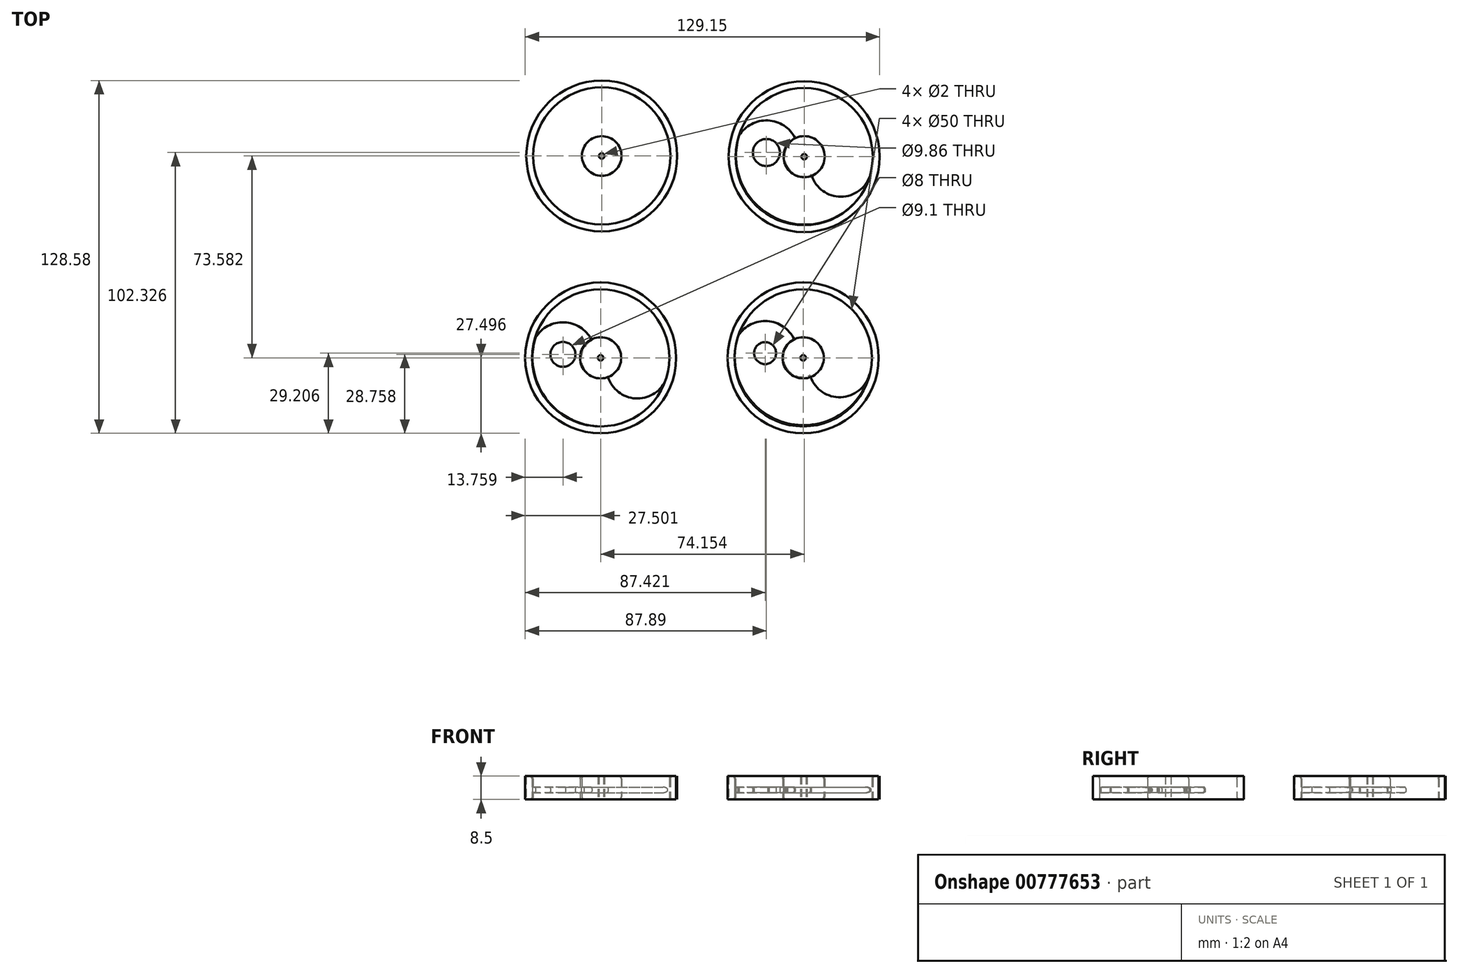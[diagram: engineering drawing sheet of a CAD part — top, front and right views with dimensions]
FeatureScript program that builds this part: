
annotation { "Feature Type Name" : "Feature", "Feature Type Description" : "" }
export const myFeature = defineFeature(function(context is Context, id is Id, definition is map)
    precondition{}
    {
        {
            var Q0;
            Q0=qCreatedBy(makeId("Top.planeOp"),FACE);
            var sketch = newSketch(context, id + "F0", { "sketchPlane" : qUnion([Q0])});
            skCircle(sketch, "E0", {"center": v(-36.84, 37.34) * mm, "radius": 27.5 * mm});
            skCircle(sketch, "E1", {"center": v(36.9, 37.09) * mm, "radius": 27.5 * mm});
            skCircle(sketch, "E2", {"center": v(36.55, -36.24) * mm, "radius": 27.5 * mm});
            skCircle(sketch, "E3", {"center": v(-37.25, -36.24) * mm, "radius": 27.5 * mm});
            skCircle(sketch, "E4", {"center": v(-36.84, 37.34) * mm, "radius": 25 * mm});
            skCircle(sketch, "E5", {"center": v(36.9, 37.09) * mm, "radius": 25 * mm});
            skCircle(sketch, "E6", {"center": v(-37.25, -36.24) * mm, "radius": 25 * mm});
            skCircle(sketch, "E7", {"center": v(36.55, -36.24) * mm, "radius": 25 * mm});
            skCircle(sketch, "E8", {"center": v(-36.84, 37.34) * mm, "radius": 7.22 * mm});
            skCircle(sketch, "E9", {"center": v(-36.84, 37.34) * mm, "radius": 1 * mm});
            skCircle(sketch, "E10", {"center": v(36.9, 37.09) * mm, "radius": 7.5 * mm});
            skCircle(sketch, "E11", {"center": v(-37.25, -36.24) * mm, "radius": 7.5 * mm});
            skCircle(sketch, "E12", {"center": v(36.55, -36.24) * mm, "radius": 7.5 * mm});
            skCircle(sketch, "E13", {"center": v(-37.25, -36.24) * mm, "radius": 1 * mm});
            skCircle(sketch, "E14", {"center": v(36.55, -36.24) * mm, "radius": 1 * mm});
            skCircle(sketch, "E15", {"center": v(36.9, 37.09) * mm, "radius": 1 * mm});
            skCircle(sketch, "E16", {"center": v(-36.84, 37.34) * mm, "radius": 24.87 * mm});
            skSolve(sketch);
        }
        {
            var Q0;
            Q0 = qSketchRegion(id + "F0", true);
            var Q1;
            Q1=makeQuery(id+"F0.imprint","IMPRINT",FACE,{"disambiguationData":[TD([[makeQuery(id+"F0.imprint","IMPRINT",EDGE,{"derivedFrom":sQuery(id+"F0.wireOp",EDGE,"E8")}),1.0]])]});
            var Q2;
            Q2=makeQuery(id+"F0.imprint","IMPRINT",FACE,{"disambiguationData":[TD([[makeQuery(id+"F0.imprint","IMPRINT",EDGE,{"derivedFrom":sQuery(id+"F0.wireOp",EDGE,"E10")}),1.0]])]});
            var Q3;
            Q3=makeQuery(id+"F0.imprint","IMPRINT",FACE,{"disambiguationData":[TD([[makeQuery(id+"F0.imprint","IMPRINT",EDGE,{"derivedFrom":sQuery(id+"F0.wireOp",EDGE,"E12")}),1.0]])]});
            var Q4;
            Q4=makeQuery(id+"F0.imprint","IMPRINT",FACE,{"disambiguationData":[TD([[makeQuery(id+"F0.imprint","IMPRINT",EDGE,{"derivedFrom":sQuery(id+"F0.wireOp",EDGE,"E11")}),1.0]])]});
            extrude(context, id + "F1", {"entities" : qUnion([Q0, Q1, Q2, Q3, Q4]), "depth" : 5 * mm, "offsetDistance" : 25 * mm, "hasSecondDirection" : true, "secondDirectionOppositeDirection" : true, "secondDirectionDepth" : 3.5 * mm});
        }
        {
            var Q0;
            Q0=makeQuery(id+"F1.opExtrude","CAP_EDGE",EDGE,{"disambiguationData":[OSD([sQuery(id+"F0.wireOp",EDGE,"E4")])],"isStart":false});
            var Q1;
            Q1=makeQuery(id+"F1.opExtrude","CAP_EDGE",EDGE,{"disambiguationData":[OSD([sQuery(id+"F0.wireOp",EDGE,"E5")])],"isStart":false});
            var Q2;
            Q2=makeQuery(id+"F1.opExtrude","CAP_EDGE",EDGE,{"disambiguationData":[OSD([sQuery(id+"F0.wireOp",EDGE,"E7")])],"isStart":false});
            var Q3;
            Q3=makeQuery(id+"F1.opExtrude","CAP_EDGE",EDGE,{"disambiguationData":[OSD([sQuery(id+"F0.wireOp",EDGE,"E8")])],"isStart":false});
            var Q4;
            Q4=makeQuery(id+"F1.opExtrude","CAP_EDGE",EDGE,{"disambiguationData":[OSD([sQuery(id+"F0.wireOp",EDGE,"E10")])],"isStart":false});
            var Q5;
            Q5=makeQuery(id+"F1.opExtrude","CAP_EDGE",EDGE,{"disambiguationData":[OSD([sQuery(id+"F0.wireOp",EDGE,"E12")])],"isStart":false});
            var Q6;
            Q6=makeQuery(id+"F1.opExtrude","CAP_EDGE",EDGE,{"disambiguationData":[OSD([sQuery(id+"F0.wireOp",EDGE,"E11")])],"isStart":false});
            var Q7;
            Q7=makeQuery(id+"F1.opExtrude","CAP_EDGE",EDGE,{"disambiguationData":[OSD([sQuery(id+"F0.wireOp",EDGE,"E11")])],"isStart":true});
            var Q8;
            Q8=makeQuery(id+"F1.opExtrude","CAP_EDGE",EDGE,{"disambiguationData":[OSD([sQuery(id+"F0.wireOp",EDGE,"E6")])],"isStart":true});
            var Q9;
            Q9=makeQuery(id+"F1.opExtrude","CAP_EDGE",EDGE,{"disambiguationData":[OSD([sQuery(id+"F0.wireOp",EDGE,"E7")])],"isStart":true});
            var Q10;
            Q10=makeQuery(id+"F1.opExtrude","CAP_EDGE",EDGE,{"disambiguationData":[OSD([sQuery(id+"F0.wireOp",EDGE,"E5")])],"isStart":true});
            var Q11;
            Q11=makeQuery(id+"F1.opExtrude","CAP_EDGE",EDGE,{"disambiguationData":[OSD([sQuery(id+"F0.wireOp",EDGE,"E10")])],"isStart":true});
            var Q12;
            Q12=makeQuery(id+"F1.opExtrude","CAP_EDGE",EDGE,{"disambiguationData":[OSD([sQuery(id+"F0.wireOp",EDGE,"E12")])],"isStart":true});
            var Q13;
            Q13=makeQuery(id+"F1.opExtrude","CAP_EDGE",EDGE,{"disambiguationData":[OSD([sQuery(id+"F0.wireOp",EDGE,"E8")])],"isStart":true});
            var Q14;
            Q14=makeQuery(id+"F1.opExtrude","CAP_EDGE",EDGE,{"disambiguationData":[OSD([sQuery(id+"F0.wireOp",EDGE,"E6")])],"isStart":false});
            var Q15;
            Q15=makeQuery(id+"F1.opExtrude","CAP_EDGE",EDGE,{"disambiguationData":[OSD([sQuery(id+"F0.wireOp",EDGE,"E4")])],"isStart":true});
            fillet(context, id + "F2", {"entities" : qUnion([Q0, Q1, Q2, Q3, Q4, Q5, Q6, Q7, Q8, Q9, Q10, Q11, Q12, Q13, Q14, Q15]), "radius" : 1 * mm, "tangentPropagation" : true, "allowEdgeOverflow" : false});
        }
        {
            var Q0;
            Q0=qCreatedBy(makeId("Top.planeOp"),FACE);
            var sketch = newSketch(context, id + "F3", { "sketchPlane" : qUnion([Q0])});
            skArc(sketch, "E17", {"start": v(39.54, 30.51) * mm, "mid": v(50.51, 22.5) * mm, "end": v(61.15, 30.94) * mm});
            skArc(sketch, "E18", {"start": v(33.7, 43.68) * mm, "mid": v(23.79, 50.28) * mm, "end": v(13.22, 44.81) * mm});
            skArc(sketch, "E19", {"start": v(13.22, 44.81) * mm, "mid": v(13.67, 28.53) * mm, "end": v(24.09, 16.02) * mm});
            skArc(sketch, "E20", {"start": v(24.09, 16.02) * mm, "mid": v(46.4, 14.1) * mm, "end": v(61.15, 30.94) * mm});
            skArc(sketch, "E21", {"start": v(30.86, 33.25) * mm, "mid": v(34.68, 30.25) * mm, "end": v(39.54, 30.51) * mm});
            skArc(sketch, "E22", {"start": v(33.7, 43.68) * mm, "mid": v(30.07, 39.06) * mm, "end": v(30.86, 33.25) * mm});
            skCircle(sketch, "E23", {"center": v(23.14, 38.59) * mm, "radius": 4.93 * mm});
            skSolve(sketch);
        }
        {
            var Q0;
            Q0 = qSketchRegion(id + "F3", true);
            extrude(context, id + "F4", {"entities" : qUnion([Q0]), "depth" : 1 * mm, "offsetDistance" : 25 * mm, "hasSecondDirection" : true, "secondDirectionOppositeDirection" : true, "secondDirectionDepth" : 1 * mm});
        }
        {
            var Q0;
            Q0=qCreatedBy(makeId("Top.planeOp"),FACE);
            var sketch = newSketch(context, id + "F5", { "sketchPlane" : qUnion([Q0])});
            skArc(sketch, "E24", {"start": v(-34.6, -43.06) * mm, "mid": v(-23.62, -51.08) * mm, "end": v(-12.98, -42.62) * mm});
            skArc(sketch, "E25", {"start": v(-40.44, -29.9) * mm, "mid": v(-50.34, -23.28) * mm, "end": v(-60.92, -28.76) * mm});
            skArc(sketch, "E26", {"start": v(-60.92, -28.76) * mm, "mid": v(-60.46, -45.03) * mm, "end": v(-50.04, -57.55) * mm});
            skArc(sketch, "E27", {"start": v(-50.04, -57.55) * mm, "mid": v(-27.73, -59.47) * mm, "end": v(-12.98, -42.62) * mm});
            skArc(sketch, "E28", {"start": v(-43.27, -40.32) * mm, "mid": v(-39.45, -43.32) * mm, "end": v(-34.6, -43.06) * mm});
            skArc(sketch, "E29", {"start": v(-40.44, -29.9) * mm, "mid": v(-44.06, -34.5) * mm, "end": v(-43.27, -40.32) * mm});
            skCircle(sketch, "E30", {"center": v(-51, -34.98) * mm, "radius": 4.55 * mm});
            skSolve(sketch);
        }
        {
            var Q0;
            Q0 = qSketchRegion(id + "F5", true);
            extrude(context, id + "F6", {"entities" : qUnion([Q0]), "depth" : 1 * mm, "offsetDistance" : 25 * mm, "hasSecondDirection" : true, "secondDirectionOppositeDirection" : true, "secondDirectionDepth" : 1 * mm});
        }
        {
            var Q0;
            Q0=qCreatedBy(makeId("Top.planeOp"),FACE);
            var sketch = newSketch(context, id + "F7", { "sketchPlane" : qUnion([Q0])});
            skArc(sketch, "E31", {"start": v(39.07, -42.6) * mm, "mid": v(50.04, -50.63) * mm, "end": v(60.69, -42.18) * mm});
            skArc(sketch, "E32", {"start": v(33.22, -29.44) * mm, "mid": v(23.32, -22.84) * mm, "end": v(12.75, -28.3) * mm});
            skArc(sketch, "E33", {"start": v(12.75, -28.3) * mm, "mid": v(13.2, -44.59) * mm, "end": v(23.62, -57.1) * mm});
            skArc(sketch, "E34", {"start": v(23.62, -57.1) * mm, "mid": v(45.93, -59.02) * mm, "end": v(60.69, -42.18) * mm});
            skArc(sketch, "E35", {"start": v(30.4, -39.87) * mm, "mid": v(34.21, -42.87) * mm, "end": v(39.07, -42.6) * mm});
            skArc(sketch, "E36", {"start": v(33.22, -29.44) * mm, "mid": v(29.6, -34.06) * mm, "end": v(30.4, -39.87) * mm});
            skCircle(sketch, "E37", {"center": v(22.67, -34.53) * mm, "radius": 4 * mm});
            skSolve(sketch);
        }
        {
            var Q0;
            Q0 = qSketchRegion(id + "F7", true);
            extrude(context, id + "F8", {"entities" : qUnion([Q0]), "depth" : 1 * mm, "offsetDistance" : 25 * mm, "hasSecondDirection" : true, "secondDirectionOppositeDirection" : true, "secondDirectionDepth" : 1 * mm});
        }
        {
            var Q0;
            Q0=makeQuery(id+"F6.opExtrude","CAP_EDGE",EDGE,{"disambiguationData":[OSD([sQuery(id+"F5.wireOp",EDGE,"E24")])],"isStart":true});
            var Q1;
            Q1=makeQuery(id+"F6.opExtrude","CAP_EDGE",EDGE,{"disambiguationData":[OSD([sQuery(id+"F5.wireOp",EDGE,"E24")])],"isStart":false});
            var Q2;
            Q2=makeQuery(id+"F6.opExtrude","CAP_EDGE",EDGE,{"disambiguationData":[OSD([sQuery(id+"F5.wireOp",EDGE,"E25")])],"isStart":true});
            var Q3;
            Q3=makeQuery(id+"F6.opExtrude","CAP_EDGE",EDGE,{"disambiguationData":[OSD([sQuery(id+"F5.wireOp",EDGE,"E25")])],"isStart":false});
            var Q4;
            Q4=makeQuery(id+"F8.opExtrude","CAP_EDGE",EDGE,{"disambiguationData":[OSD([sQuery(id+"F7.wireOp",EDGE,"E31")])],"isStart":true});
            var Q5;
            Q5=makeQuery(id+"F8.opExtrude","CAP_EDGE",EDGE,{"disambiguationData":[OSD([sQuery(id+"F7.wireOp",EDGE,"E31")])],"isStart":false});
            var Q6;
            Q6=makeQuery(id+"F8.opExtrude","CAP_EDGE",EDGE,{"disambiguationData":[OSD([sQuery(id+"F7.wireOp",EDGE,"E32")])],"isStart":true});
            var Q7;
            Q7=makeQuery(id+"F8.opExtrude","CAP_EDGE",EDGE,{"disambiguationData":[OSD([sQuery(id+"F7.wireOp",EDGE,"E32")])],"isStart":false});
            var Q8;
            Q8=makeQuery(id+"F6.opExtrude","CAP_EDGE",EDGE,{"disambiguationData":[OSD([sQuery(id+"F5.wireOp",EDGE,"E30")])],"isStart":true});
            var Q9;
            Q9=makeQuery(id+"F6.opExtrude","CAP_EDGE",EDGE,{"disambiguationData":[OSD([sQuery(id+"F5.wireOp",EDGE,"E30")])],"isStart":false});
            var Q10;
            Q10=makeQuery(id+"F8.opExtrude","CAP_EDGE",EDGE,{"disambiguationData":[OSD([sQuery(id+"F7.wireOp",EDGE,"E37")])],"isStart":true});
            var Q11;
            Q11=makeQuery(id+"F8.opExtrude","CAP_EDGE",EDGE,{"disambiguationData":[OSD([sQuery(id+"F7.wireOp",EDGE,"E37")])],"isStart":false});
            var Q12;
            Q12=makeQuery(id+"F0Lw73LTv5gNUkS_8.opExtrude","CAP_EDGE",EDGE,{"disambiguationData":[OSD([sQuery(id+"FaSVQBoLKEiFSzY_8.wireOp",EDGE,"Rkogj6an-mIMs-5Vwq-ItiI-HnNTVvaIVaFF")])],"isStart":true});
            var Q13;
            Q13=makeQuery(id+"F0Lw73LTv5gNUkS_8.opExtrude","CAP_EDGE",EDGE,{"disambiguationData":[OSD([sQuery(id+"FaSVQBoLKEiFSzY_8.wireOp",EDGE,"0PIxKRfm-EENJ-GXSr-GtYf-4HL3wGRdEfpe")])],"isStart":true});
            var Q14;
            Q14=makeQuery(id+"F0Lw73LTv5gNUkS_8.opExtrude","CAP_EDGE",EDGE,{"disambiguationData":[OSD([sQuery(id+"FaSVQBoLKEiFSzY_8.wireOp",EDGE,"vxq344Cw-Kjq4-zHd9-gQkO-X8a2N7v6S6Nq")])],"isStart":true});
            var Q15;
            Q15=makeQuery(id+"F4.opExtrude","CAP_EDGE",EDGE,{"disambiguationData":[OSD([sQuery(id+"F3.wireOp",EDGE,"E23")])],"isStart":true});
            var Q16;
            Q16=makeQuery(id+"F4.opExtrude","CAP_EDGE",EDGE,{"disambiguationData":[OSD([sQuery(id+"F3.wireOp",EDGE,"E18")])],"isStart":true});
            var Q17;
            Q17=makeQuery(id+"F4.opExtrude","CAP_EDGE",EDGE,{"disambiguationData":[OSD([sQuery(id+"F3.wireOp",EDGE,"E17")])],"isStart":true});
            var Q18;
            Q18=makeQuery(id+"F0Lw73LTv5gNUkS_8.opExtrude","CAP_EDGE",EDGE,{"disambiguationData":[OSD([sQuery(id+"FaSVQBoLKEiFSzY_8.wireOp",EDGE,"vxq344Cw-Kjq4-zHd9-gQkO-X8a2N7v6S6Nq")])],"isStart":false});
            var Q19;
            Q19=makeQuery(id+"F0Lw73LTv5gNUkS_8.opExtrude","CAP_EDGE",EDGE,{"disambiguationData":[OSD([sQuery(id+"FaSVQBoLKEiFSzY_8.wireOp",EDGE,"0PIxKRfm-EENJ-GXSr-GtYf-4HL3wGRdEfpe")])],"isStart":false});
            var Q20;
            Q20=makeQuery(id+"F0Lw73LTv5gNUkS_8.opExtrude","CAP_EDGE",EDGE,{"disambiguationData":[OSD([sQuery(id+"FaSVQBoLKEiFSzY_8.wireOp",EDGE,"Rkogj6an-mIMs-5Vwq-ItiI-HnNTVvaIVaFF")])],"isStart":false});
            var Q21;
            Q21=makeQuery(id+"F4.opExtrude","CAP_EDGE",EDGE,{"disambiguationData":[OSD([sQuery(id+"F3.wireOp",EDGE,"E18")])],"isStart":false});
            var Q22;
            Q22=makeQuery(id+"F4.opExtrude","CAP_EDGE",EDGE,{"disambiguationData":[OSD([sQuery(id+"F3.wireOp",EDGE,"E23")])],"isStart":false});
            var Q23;
            Q23=makeQuery(id+"F4.opExtrude","CAP_EDGE",EDGE,{"disambiguationData":[OSD([sQuery(id+"F3.wireOp",EDGE,"E17")])],"isStart":false});
            fillet(context, id + "F9", {"entities" : qUnion([Q0, Q1, Q2, Q3, Q4, Q5, Q6, Q7, Q8, Q9, Q10, Q11, Q12, Q13, Q14, Q15, Q16, Q17, Q18, Q19, Q20, Q21, Q22, Q23]), "radius" : .5 * mm, "tangentPropagation" : true, "allowEdgeOverflow" : false});
        }
    });
